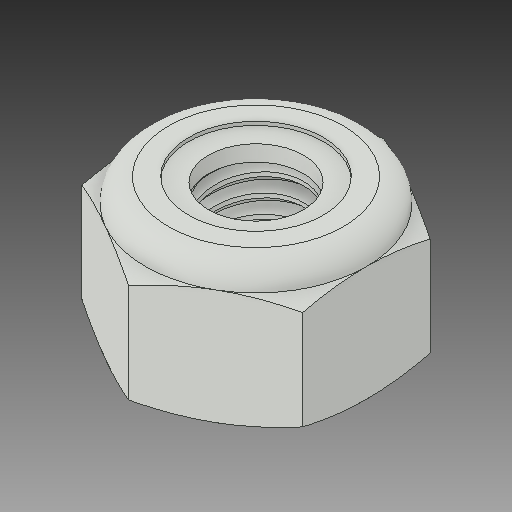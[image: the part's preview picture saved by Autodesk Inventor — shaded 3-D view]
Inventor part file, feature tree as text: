
AUTODESK INVENTOR PART (.ipt)
format: ipt  version: 2018 (Build 220112000, 112)  size: 333,312 bytes
history: native  units: in
note: dims shown in document units (in); Inventor stores cm internally (conversion verified against a paired STEP export)
features: other x1, revolve x1
ambient origin geometry x8: Origin, YZ Plane, XZ Plane, XY Plane, X Axis, Y Axis, Z Axis, Center Point
bodies: Solid1 (feature_tree), Solid2 (feature_tree)
feature tree (2):
  other  "Cut-Revolve4"
  revolve  "Revolve2"  [1 undecoded]
note: 1 required parameter value undecoded (feature->parameter linkage not recoverable at this tier; creation-order binding heuristic only, values carry confidence <= 0.55)
